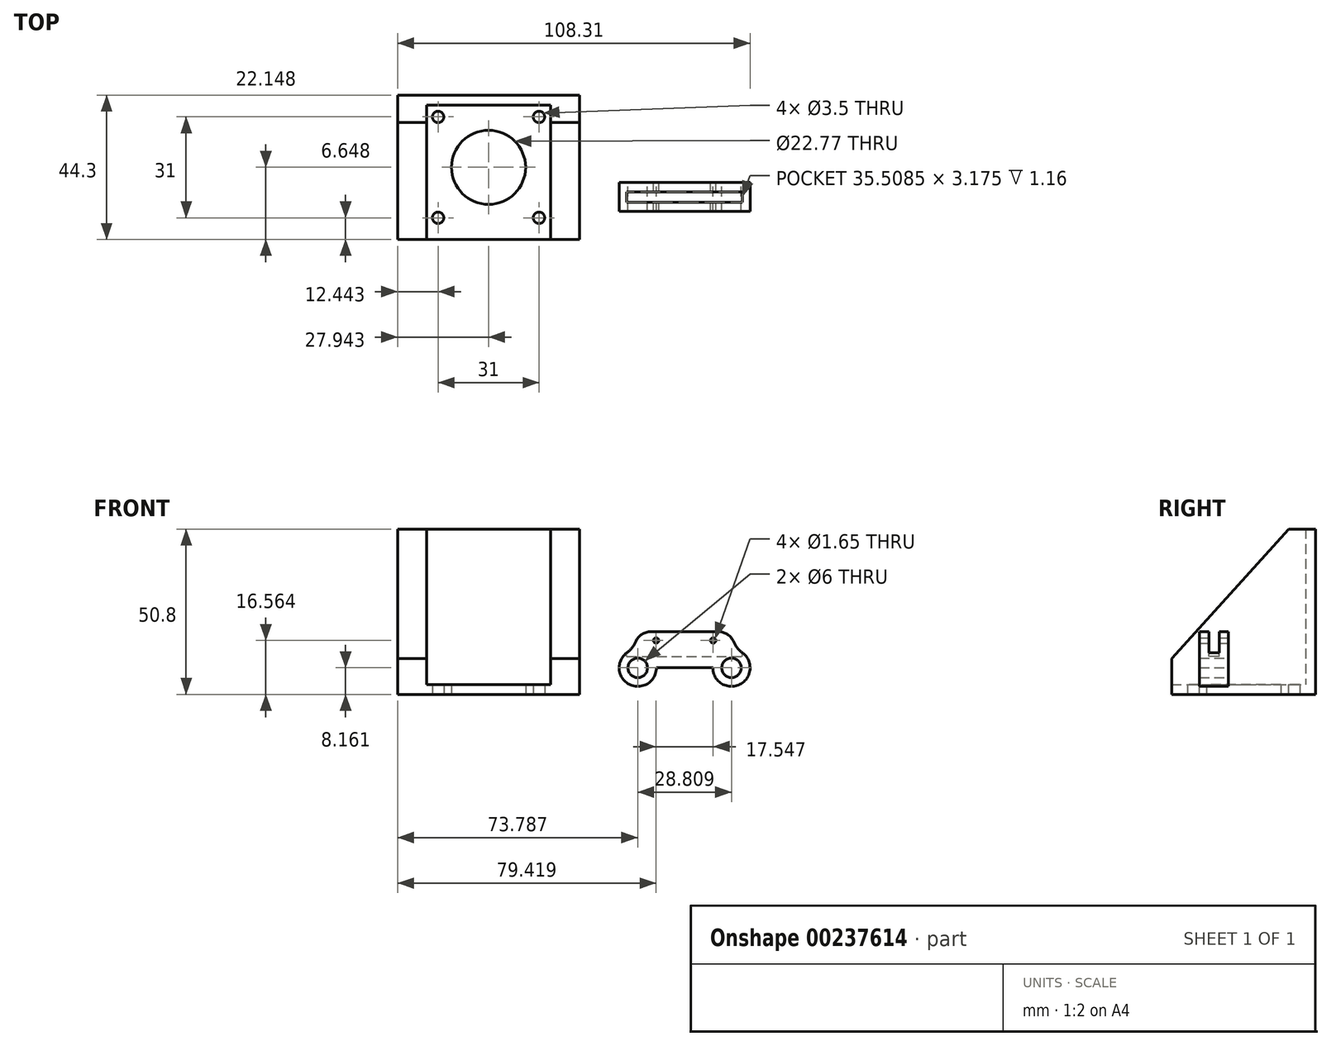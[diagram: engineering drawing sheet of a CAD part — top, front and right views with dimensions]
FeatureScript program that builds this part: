
annotation { "Feature Type Name" : "Feature", "Feature Type Description" : "" }
export const myFeature = defineFeature(function(context is Context, id is Id, definition is map)
    precondition{}
    {
        {
            var Q0;
            Q0=qCreatedBy(makeId("Top.planeOp"),FACE);
            var sketch = newSketch(context, id + "F0", { "sketchPlane" : qUnion([Q0])});
            skLineSegment(sketch, "E0.bottom", {"start": v(-2.5, -14.37) * mm, "end": v(-40.6, -14.37) * mm});
            skLineSegment(sketch, "E0.top", {"start": v(-2.5, 23.73) * mm, "end": v(-40.6, 23.73) * mm});
            skLineSegment(sketch, "E0.left", {"start": v(-2.5, -14.37) * mm, "end": v(-2.5, 23.73) * mm});
            skLineSegment(sketch, "E0.right", {"start": v(-40.6, -14.37) * mm, "end": v(-40.6, 23.73) * mm});
            skPoint(sketch, "E0.middle", {"position": v(-21.55, 4.68) * mm});
            skCircle(sketch, "E1", {"center": v(-21.55, 4.68) * mm, "radius": 11.38 * mm});
            skCircle(sketch, "E2", {"center": v(-37.05, 20.18) * mm, "radius": 1.75 * mm});
            skCircle(sketch, "E3", {"center": v(-6.05, 20.18) * mm, "radius": 1.75 * mm});
            skCircle(sketch, "E4", {"center": v(-6.05, -10.82) * mm, "radius": 1.75 * mm});
            skCircle(sketch, "E5", {"center": v(-37.05, -10.82) * mm, "radius": 1.75 * mm});
            skLineSegment(sketch, "E6", {"start": v(-37.05, 20.18) * mm, "end": v(-6.05, 20.18) * mm, "construction": true});
            skLineSegment(sketch, "E7", {"start": v(-6.05, -10.82) * mm, "end": v(-6.05, 20.18) * mm, "construction": true});
            skLineSegment(sketch, "E8", {"start": v(-37.05, 20.18) * mm, "end": v(-37.05, -10.82) * mm, "construction": true});
            skLineSegment(sketch, "E9", {"start": v(-6.05, -10.82) * mm, "end": v(-37.05, -10.82) * mm, "construction": true});
            skPoint(sketch, "E10", {"position": v(-21.55, 20.18) * mm});
            skPoint(sketch, "E11", {"position": v(-37.05, 4.68) * mm});
            skLineSegment(sketch, "E12.bottom", {"start": v(-49.49, 26.83) * mm, "end": v(6.4, 26.83) * mm});
            skLineSegment(sketch, "E12.top", {"start": v(-49.49, -17.47) * mm, "end": v(6.4, -17.47) * mm});
            skLineSegment(sketch, "E12.left", {"start": v(-49.49, 26.83) * mm, "end": v(-49.49, -17.47) * mm});
            skLineSegment(sketch, "E12.right", {"start": v(6.4, 26.83) * mm, "end": v(6.4, -17.47) * mm});
            skLineSegment(sketch, "E13", {"start": v(-40.6, -14.37) * mm, "end": v(-40.6, -17.47) * mm});
            skLineSegment(sketch, "E14", {"start": v(-2.5, -14.37) * mm, "end": v(-2.5, -17.47) * mm});
            skSolve(sketch);
        }
        {
            var Q0;
            Q0=makeQuery(id+"F0.imprint","IMPRINT",FACE,{"disambiguationData":[TD([[makeQuery(id+"F0.imprint","IMPRINT",EDGE,{"derivedFrom":sQuery(id+"F0.wireOp",EDGE,"E0.bottom")}),-1.0]])]});
            var Q1;
            Q1=makeQuery(id+"F0.imprint","IMPRINT",FACE,{"disambiguationData":[TD([[makeQuery(id+"F0.imprint","IMPRINT",EDGE,{"derivedFrom":sQuery(id+"F0.wireOp",EDGE,"E0.bottom")}),1.0]])]});
            extrude(context, id + "F1", {"entities" : qUnion([Q0, Q1]), "depth" : 3 * mm});
        }
        {
            var Q0;
            Q0=makeQuery(id+"F0.imprint","IMPRINT",FACE,{"disambiguationData":[TD([[makeQuery(id+"F0.imprint","IMPRINT",EDGE,{"derivedFrom":sQuery(id+"F0.wireOp",EDGE,"E0.top")}),-1.0]])]});
            extrude(context, id + "F2", {"entities" : qUnion([Q0]), "operationType" : NewBodyOperationType.ADD, "depth" : 50.8 * mm});
        }
        {
            var Q0;
            Q0=makeQuery(id+"F2.opExtrude","SWEPT_FACE",FACE,{"disambiguationData":[OSD([sQuery(id+"F0.wireOp",EDGE,"E12.left")])]});
            var sketch = newSketch(context, id + "F3", { "sketchPlane" : qUnion([Q0])});
            skLineSegment(sketch, "E15", {"start": v(-18.51, 50.8) * mm, "end": v(17.47, 10.97) * mm});
            skLineSegment(sketch, "E16", {"start": v(17.47, 50.8) * mm, "end": v(17.47, 10.97) * mm});
            skLineSegment(sketch, "E17", {"start": v(-18.51, 50.8) * mm, "end": v(17.47, 50.8) * mm});
            skSolve(sketch);
        }
        {
            var Q0;
            Q0 = qSketchRegion(id + "F3", true);
            var Q1;
            Q1=makeQuery(id+"F2.opExtrude","SWEPT_FACE",FACE,{"disambiguationData":[OSD([sQuery(id+"F0.wireOp",EDGE,"E12.right")])]});
            extrude(context, id + "F4", {"entities" : qUnion([Q0]), "operationType" : NewBodyOperationType.REMOVE, "endBound" : BoundingType.UP_TO_SURFACE, "oppositeDirection" : true, "endBoundEntityFace" : qUnion([Q1]), "depth" : 25.4 * mm});
        }
        {
            var Q0;
            Q0=qCreatedBy(makeId("Front.planeOp"),FACE);
            var sketch = newSketch(context, id + "F5", { "sketchPlane" : qUnion([Q0])});
            skCircle(sketch, "E18", {"center": v(24.3, 8.16) * mm, "radius": 3 * mm});
            skArc(sketch, "E19", {"start": v(24.3, 13.88) * mm, "mid": v(20.26, 4.12) * mm, "end": v(30.01, 8.16) * mm});
            skCircle(sketch, "E20", {"center": v(53.1, 8.16) * mm, "radius": 3 * mm});
            skArc(sketch, "E21", {"start": v(47.4, 8.16) * mm, "mid": v(57.15, 4.12) * mm, "end": v(53.1, 13.88) * mm});
            skLineSegment(sketch, "E22.top", {"start": v(24.3, 19.25) * mm, "end": v(53.1, 19.25) * mm});
            skLineSegment(sketch, "E22.left", {"start": v(24.3, 13.88) * mm, "end": v(24.3, 19.25) * mm});
            skLineSegment(sketch, "E22.right", {"start": v(53.1, 13.88) * mm, "end": v(53.1, 19.25) * mm});
            skLineSegment(sketch, "E23.trimOffspring", {"start": v(30.01, 8.16) * mm, "end": v(47.4, 8.16) * mm});
            skCircle(sketch, "E24", {"center": v(29.93, 16.56) * mm, "radius": 0.82 * mm});
            skPoint(sketch, "E24.centerSnap0", {"position": v(24.3, 16.56) * mm});
            skCircle(sketch, "E25", {"center": v(47.48, 16.56) * mm, "radius": 0.82 * mm});
            skPoint(sketch, "E25.centerSnap0", {"position": v(53.1, 16.56) * mm});
            skLineSegment(sketch, "E26", {"start": v(24.3, 16.56) * mm, "end": v(29.93, 16.56) * mm, "construction": true});
            skLineSegment(sketch, "E27", {"start": v(47.48, 16.56) * mm, "end": v(53.1, 16.56) * mm, "construction": true});
            skSolve(sketch);
        }
        {
            var Q0;
            Q0 = qSketchRegion(id + "F5", true);
            extrude(context, id + "F6", {"entities" : qUnion([Q0]), "depth" : 8.9 * mm});
        }
        {
            var Q0;
            Q0=makeQuery(id+"F6.opExtrude","SWEPT_EDGE",EDGE,{"disambiguationData":[OSD([sQuery(id+"F5.wireOp",EDGE,"E19"),sQuery(id+"F5.wireOp",EDGE,"E22.left")])]});
            var Q1;
            Q1=makeQuery(id+"F6.opExtrude","SWEPT_EDGE",EDGE,{"disambiguationData":[OSD([sQuery(id+"F5.wireOp",EDGE,"E21"),sQuery(id+"F5.wireOp",EDGE,"E22.right")])]});
            fillet(context, id + "F7", {"entities" : qUnion([Q0, Q1]), "radius" : 8.1 * mm, "tangentPropagation" : true, "allowEdgeOverflow" : false});
        }
        {
            var Q0;
            Q0=makeQuery(id+"F7.opFillet","BLEND_EDGE",EDGE,{"blendedFrom":[makeQuery(id+"F6.opExtrude","SWEPT_EDGE",EDGE,{"disambiguationData":[OSD([sQuery(id+"F5.wireOp",EDGE,"E19"),sQuery(id+"F5.wireOp",EDGE,"E22.left")])]}),makeQuery(id+"F6.opExtrude","SWEPT_FACE",FACE,{"disambiguationData":[OSD([sQuery(id+"F5.wireOp",EDGE,"E22.top")])]})],"blendedInto":[makeQuery(id+"F6.opExtrude","SWEPT_FACE",FACE,{"disambiguationData":[OSD([sQuery(id+"F5.wireOp",EDGE,"E22.top")])]})]});
            var Q1;
            Q1=makeQuery(id+"F7.opFillet","BLEND_EDGE",EDGE,{"blendedFrom":[makeQuery(id+"F6.opExtrude","SWEPT_EDGE",EDGE,{"disambiguationData":[OSD([sQuery(id+"F5.wireOp",EDGE,"E21"),sQuery(id+"F5.wireOp",EDGE,"E22.right")])]}),makeQuery(id+"F6.opExtrude","SWEPT_FACE",FACE,{"disambiguationData":[OSD([sQuery(id+"F5.wireOp",EDGE,"E22.top")])]})],"blendedInto":[makeQuery(id+"F6.opExtrude","SWEPT_FACE",FACE,{"disambiguationData":[OSD([sQuery(id+"F5.wireOp",EDGE,"E22.top")])]})]});
            fillet(context, id + "F8", {"entities" : qUnion([Q0, Q1]), "radius" : 5.08 * mm, "tangentPropagation" : true, "allowEdgeOverflow" : false});
        }
        {
            var Q0;
            Q0=makeQuery(id+"F6.opExtrude","SWEPT_FACE",FACE,{"disambiguationData":[OSD([sQuery(id+"F5.wireOp",EDGE,"E22.top")])]});
            var sketch = newSketch(context, id + "F9", { "sketchPlane" : qUnion([Q0])});
            skLineSegment(sketch, "E28.bottom", {"start": v(20.95, -2.86) * mm, "end": v(56.46, -2.86) * mm});
            skLineSegment(sketch, "E28.top", {"start": v(20.95, -6.03) * mm, "end": v(56.46, -6.03) * mm});
            skLineSegment(sketch, "E28.left", {"start": v(20.95, -2.86) * mm, "end": v(20.95, -6.03) * mm});
            skLineSegment(sketch, "E28.right", {"start": v(56.46, -2.86) * mm, "end": v(56.46, -6.03) * mm});
            skPoint(sketch, "E28.middle", {"position": v(38.7, -4.45) * mm});
            skPoint(sketch, "E28.middle.positionSnap0", {"position": v(28.32, -4.45) * mm});
            skPoint(sketch, "E28.middle.positionSnap1", {"position": v(38.7, 0) * mm});
            skPoint(sketch, "E28.centerSnap0", {"position": v(28.32, -4.45) * mm});
            skPoint(sketch, "E28.centerSnap1", {"position": v(38.7, 0) * mm});
            skLineSegment(sketch, "E29.0", {"start": v(20.95, -8.9) * mm, "end": v(20.95, 0) * mm});
            skSolve(sketch);
        }
        {
            var Q0;
            Q0 = qSketchRegion(id + "F9", true);
            extrude(context, id + "F10", {"entities" : qUnion([Q0]), "operationType" : NewBodyOperationType.REMOVE, "oppositeDirection" : true, "depth" : 7.62 * mm});
        }
    });
